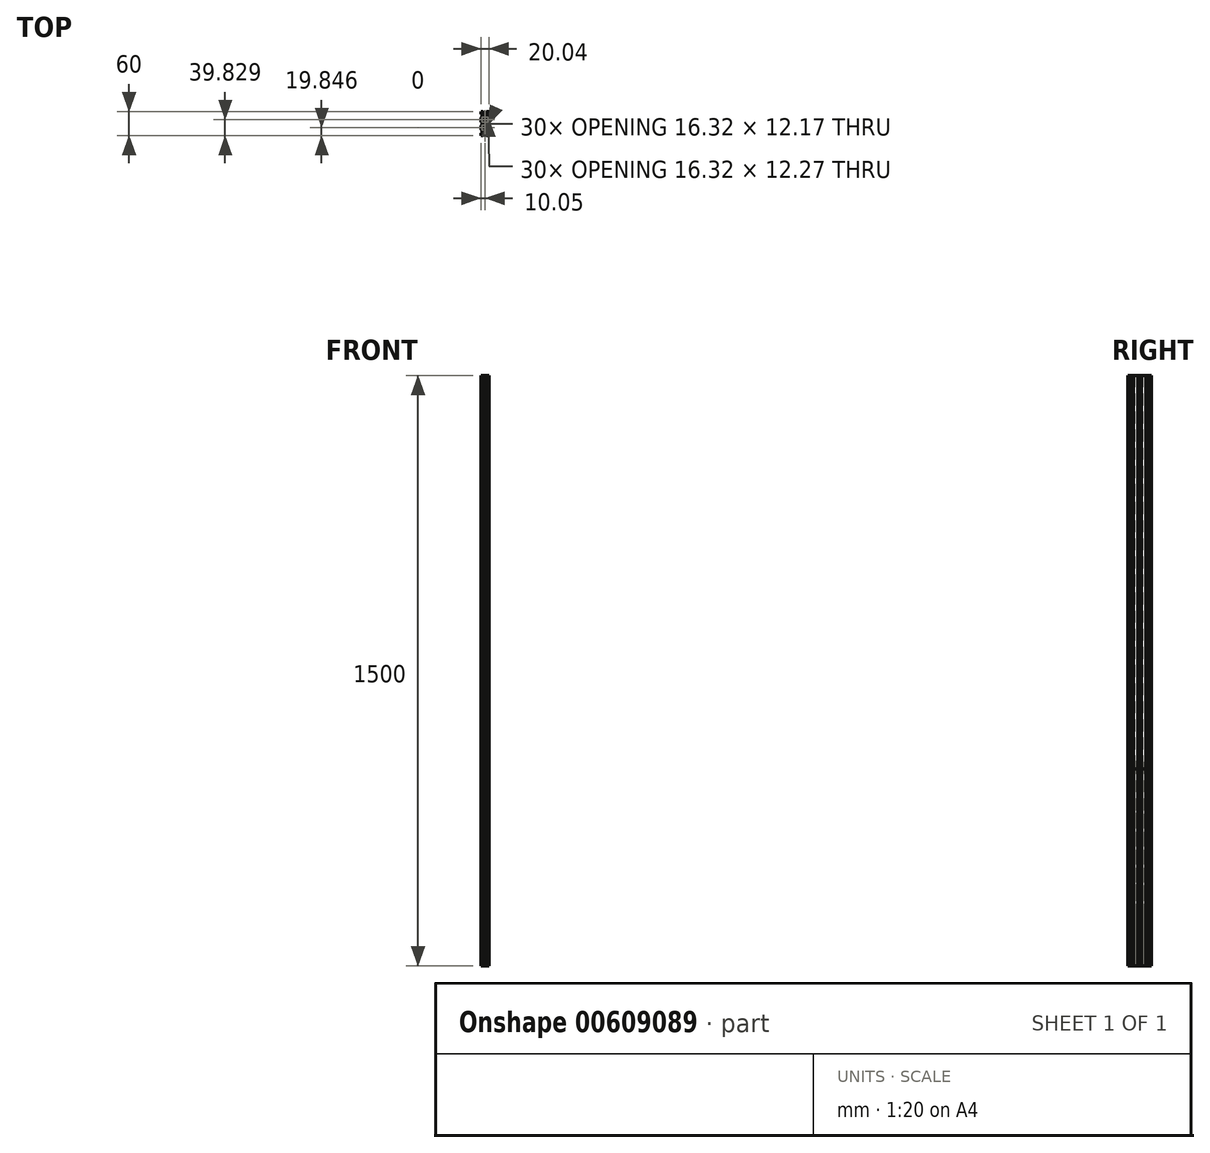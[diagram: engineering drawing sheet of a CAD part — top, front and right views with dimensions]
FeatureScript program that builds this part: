
annotation { "Feature Type Name" : "Feature", "Feature Type Description" : "" }
export const myFeature = defineFeature(function(context is Context, id is Id, definition is map)
    precondition{}
    {
        {
            var Q0;
            Q0=qCreatedBy(makeId("Top.planeOp"),FACE);
            var sketch = newSketch(context, id + "F0", { "sketchPlane" : qUnion([Q0])});
            skLineSegment(sketch, "E0", {"start": v(8.82, 10) * mm, "end": v(5.5, 10) * mm});
            skLineSegment(sketch, "E1", {"start": v(5.5, 10) * mm, "end": v(4.41, 10) * mm});
            skLineSegment(sketch, "E2", {"start": v(4.41, 10) * mm, "end": v(2.4, 8) * mm});
            skLineSegment(sketch, "E3", {"start": v(2.4, 8) * mm, "end": v(5.5, 8) * mm});
            skLineSegment(sketch, "E4", {"start": v(5.5, 8) * mm, "end": v(5.5, 6.68) * mm});
            skLineSegment(sketch, "E5", {"start": v(5.5, 6.68) * mm, "end": v(2.56, 3.74) * mm});
            skLineSegment(sketch, "E6", {"start": v(2.56, 3.74) * mm, "end": v(-2.91, 3.74) * mm});
            skLineSegment(sketch, "E7", {"start": v(-2.91, 3.74) * mm, "end": v(-5.5, 6.33) * mm});
            skLineSegment(sketch, "E8", {"start": v(-5.5, 6.33) * mm, "end": v(-5.5, 8) * mm});
            skLineSegment(sketch, "E9", {"start": v(-5.5, 8) * mm, "end": v(-2.76, 8) * mm});
            skLineSegment(sketch, "E10", {"start": v(-2.76, 8) * mm, "end": v(-4.77, 10) * mm});
            skLineSegment(sketch, "E11", {"start": v(-4.77, 10) * mm, "end": v(-5.5, 10) * mm});
            skLineSegment(sketch, "E12", {"start": v(-5.5, 10) * mm, "end": v(-9.17, 10) * mm});
            skLineSegment(sketch, "E13", {"start": v(-9.17, 10) * mm, "end": v(-10, 10) * mm});
            skLineSegment(sketch, "E14", {"start": v(-10, 10) * mm, "end": v(-10, 8.46) * mm});
            skLineSegment(sketch, "E15", {"start": v(-10, 8.46) * mm, "end": v(-10, 5.5) * mm});
            skLineSegment(sketch, "E16", {"start": v(-10, 5.5) * mm, "end": v(-10, 4.32) * mm});
            skLineSegment(sketch, "E17", {"start": v(-10, 4.32) * mm, "end": v(-8.12, 2.43) * mm});
            skLineSegment(sketch, "E18", {"start": v(-8.12, 2.43) * mm, "end": v(-8.12, 5.5) * mm});
            skLineSegment(sketch, "E19", {"start": v(-8.12, 5.5) * mm, "end": v(-7.05, 5.5) * mm});
            skLineSegment(sketch, "E20", {"start": v(-7.05, 5.5) * mm, "end": v(-3.86, 2.32) * mm});
            skLineSegment(sketch, "E21", {"start": v(-3.86, 2.32) * mm, "end": v(-3.86, -2.68) * mm});
            skLineSegment(sketch, "E22", {"start": v(-3.86, -2.68) * mm, "end": v(-6.68, -5.5) * mm});
            skLineSegment(sketch, "E23", {"start": v(-6.68, -5.5) * mm, "end": v(-8.12, -5.5) * mm});
            skLineSegment(sketch, "E24", {"start": v(-8.12, -5.5) * mm, "end": v(-8.12, -2.8) * mm});
            skLineSegment(sketch, "E25", {"start": v(-8.12, -2.8) * mm, "end": v(-10, -4.68) * mm});
            skLineSegment(sketch, "E26", {"start": v(-10, -4.68) * mm, "end": v(-10, -5.5) * mm});
            skLineSegment(sketch, "E27", {"start": v(-10, -5.5) * mm, "end": v(-10, -8.82) * mm});
            skLineSegment(sketch, "E28", {"start": v(-10, -8.82) * mm, "end": v(-10, -10) * mm});
            skLineSegment(sketch, "E29", {"start": v(-10, -10) * mm, "end": v(-8.8, -10) * mm});
            skLineSegment(sketch, "E30", {"start": v(-8.8, -10) * mm, "end": v(-5.5, -10) * mm});
            skLineSegment(sketch, "E31", {"start": v(-5.5, -10) * mm, "end": v(-4.5, -10) * mm});
            skLineSegment(sketch, "E32", {"start": v(-4.5, -10) * mm, "end": v(-2.85, -8.36) * mm});
            skLineSegment(sketch, "E33", {"start": v(-2.85, -8.36) * mm, "end": v(-5.5, -8.36) * mm});
            skLineSegment(sketch, "E34", {"start": v(-5.5, -8.36) * mm, "end": v(-5.5, -6.7) * mm});
            skLineSegment(sketch, "E35", {"start": v(-5.5, -6.7) * mm, "end": v(-2.82, -4.01) * mm});
            skLineSegment(sketch, "E36", {"start": v(-2.82, -4.01) * mm, "end": v(2.47, -4.01) * mm});
            skLineSegment(sketch, "E37", {"start": v(2.47, -4.01) * mm, "end": v(5.5, -7.05) * mm});
            skLineSegment(sketch, "E38", {"start": v(5.5, -7.05) * mm, "end": v(5.5, -8.36) * mm});
            skLineSegment(sketch, "E39", {"start": v(5.5, -8.36) * mm, "end": v(2.5, -8.36) * mm});
            skLineSegment(sketch, "E40", {"start": v(2.5, -8.36) * mm, "end": v(4.14, -10) * mm});
            skLineSegment(sketch, "E41", {"start": v(4.14, -10) * mm, "end": v(5.5, -10) * mm});
            skLineSegment(sketch, "E42", {"start": v(5.5, -10) * mm, "end": v(8.46, -10) * mm});
            skLineSegment(sketch, "E43", {"start": v(8.46, -10) * mm, "end": v(10, -10) * mm});
            skLineSegment(sketch, "E44", {"start": v(10, -10) * mm, "end": v(10, -9.17) * mm});
            skLineSegment(sketch, "E45", {"start": v(10, -9.17) * mm, "end": v(10, -5.5) * mm});
            skLineSegment(sketch, "E46", {"start": v(10, -5.5) * mm, "end": v(10, -4.6) * mm});
            skLineSegment(sketch, "E47", {"start": v(10, -4.6) * mm, "end": v(8.24, -2.83) * mm});
            skLineSegment(sketch, "E48", {"start": v(8.24, -2.83) * mm, "end": v(8.24, -5.5) * mm});
            skLineSegment(sketch, "E49", {"start": v(8.24, -5.5) * mm, "end": v(6.33, -5.5) * mm});
            skLineSegment(sketch, "E50", {"start": v(6.33, -5.5) * mm, "end": v(3.9, -3.06) * mm});
            skLineSegment(sketch, "E51", {"start": v(3.9, -3.06) * mm, "end": v(3.9, 2.7) * mm});
            skLineSegment(sketch, "E52", {"start": v(3.9, 2.7) * mm, "end": v(6.7, 5.5) * mm});
            skLineSegment(sketch, "E53", {"start": v(6.7, 5.5) * mm, "end": v(8.24, 5.5) * mm});
            skLineSegment(sketch, "E54", {"start": v(8.24, 5.5) * mm, "end": v(8.24, 2.46) * mm});
            skLineSegment(sketch, "E55", {"start": v(8.24, 2.46) * mm, "end": v(10, 4.23) * mm});
            skLineSegment(sketch, "E56", {"start": v(10, 4.23) * mm, "end": v(10, 5.5) * mm});
            skLineSegment(sketch, "E57", {"start": v(10, 5.5) * mm, "end": v(10, 8.8) * mm});
            skLineSegment(sketch, "E58", {"start": v(10, 8.8) * mm, "end": v(10, 10) * mm});
            skLineSegment(sketch, "E59", {"start": v(10, 10) * mm, "end": v(8.82, 10) * mm});
            skSolve(sketch);
        }
        {
            var Q0;
            Q0=makeQuery(id+"F0.imprint","IMPRINT",FACE,{"disambiguationData":[TD([[makeQuery(id+"F0.imprint","IMPRINT",EDGE,{"derivedFrom":sQuery(id+"F0.wireOp",EDGE,"E0")}),1.0]])]});
            extrude(context, id + "F1", {"entities" : qUnion([Q0]), "depth" : 119.7 * mm, "offsetDistance" : 25 * mm});
        }
        {
            var Q0;
            Q0=qCreatedBy(makeId("Top.planeOp"),FACE);
            var sketch = newSketch(context, id + "F2", { "sketchPlane" : qUnion([Q0])});
            skLineSegment(sketch, "E60", {"start": v(8.84, 30) * mm, "end": v(5.51, 30) * mm});
            skLineSegment(sketch, "E61", {"start": v(5.51, 30) * mm, "end": v(4.42, 30) * mm});
            skLineSegment(sketch, "E62", {"start": v(4.42, 30) * mm, "end": v(2.41, 28) * mm});
            skLineSegment(sketch, "E63", {"start": v(2.41, 28) * mm, "end": v(5.51, 28) * mm});
            skLineSegment(sketch, "E64", {"start": v(5.51, 28) * mm, "end": v(5.51, 26.67) * mm});
            skLineSegment(sketch, "E65", {"start": v(5.51, 26.67) * mm, "end": v(2.56, 23.73) * mm});
            skLineSegment(sketch, "E66", {"start": v(2.56, 23.73) * mm, "end": v(-2.92, 23.73) * mm});
            skLineSegment(sketch, "E67", {"start": v(-2.92, 23.73) * mm, "end": v(-5.51, 26.32) * mm});
            skLineSegment(sketch, "E68", {"start": v(-5.51, 26.32) * mm, "end": v(-5.51, 28) * mm});
            skLineSegment(sketch, "E69", {"start": v(-5.51, 28) * mm, "end": v(-2.76, 28) * mm});
            skLineSegment(sketch, "E70", {"start": v(-2.76, 28) * mm, "end": v(-4.77, 30) * mm});
            skLineSegment(sketch, "E71", {"start": v(-4.77, 30) * mm, "end": v(-5.51, 30) * mm});
            skLineSegment(sketch, "E72", {"start": v(-5.51, 30) * mm, "end": v(-9.19, 30) * mm});
            skLineSegment(sketch, "E73", {"start": v(-9.19, 30) * mm, "end": v(-10.02, 30) * mm});
            skLineSegment(sketch, "E74", {"start": v(-10.02, 30) * mm, "end": v(-10.02, 28.45) * mm});
            skLineSegment(sketch, "E75", {"start": v(-10.02, 28.45) * mm, "end": v(-10.02, 25.5) * mm});
            skLineSegment(sketch, "E76", {"start": v(-10.02, 25.5) * mm, "end": v(-10.02, 24.3) * mm});
            skLineSegment(sketch, "E77", {"start": v(-10.02, 24.3) * mm, "end": v(-8.13, 22.42) * mm});
            skLineSegment(sketch, "E78", {"start": v(-8.13, 22.42) * mm, "end": v(-8.13, 25.5) * mm});
            skLineSegment(sketch, "E79", {"start": v(-8.13, 25.5) * mm, "end": v(-7.06, 25.5) * mm});
            skLineSegment(sketch, "E80", {"start": v(-7.06, 25.5) * mm, "end": v(-3.87, 22.3) * mm});
            skLineSegment(sketch, "E81", {"start": v(-3.87, 22.3) * mm, "end": v(-3.87, 17.3) * mm});
            skLineSegment(sketch, "E82", {"start": v(-3.87, 17.3) * mm, "end": v(-6.7, 14.47) * mm});
            skLineSegment(sketch, "E83", {"start": v(-6.7, 14.47) * mm, "end": v(-8.13, 14.47) * mm});
            skLineSegment(sketch, "E84", {"start": v(-8.13, 14.47) * mm, "end": v(-8.13, 17.18) * mm});
            skLineSegment(sketch, "E85", {"start": v(-8.13, 17.18) * mm, "end": v(-10.02, 15.3) * mm});
            skLineSegment(sketch, "E86", {"start": v(-10.02, 15.3) * mm, "end": v(-10.02, 14.47) * mm});
            skLineSegment(sketch, "E87", {"start": v(-10.02, 14.47) * mm, "end": v(-10.02, 11.15) * mm});
            skLineSegment(sketch, "E88", {"start": v(-10.02, 11.15) * mm, "end": v(-10.02, 9.97) * mm});
            skLineSegment(sketch, "E89", {"start": v(-10.02, 9.97) * mm, "end": v(-10.02, 8.42) * mm});
            skLineSegment(sketch, "E90", {"start": v(-10.02, 8.42) * mm, "end": v(-10.02, 5.46) * mm});
            skLineSegment(sketch, "E91", {"start": v(-10.02, 5.46) * mm, "end": v(-10.02, 4.27) * mm});
            skLineSegment(sketch, "E92", {"start": v(-10.02, 4.27) * mm, "end": v(-8.13, 2.38) * mm});
            skLineSegment(sketch, "E93", {"start": v(-8.13, 2.38) * mm, "end": v(-8.13, 5.46) * mm});
            skLineSegment(sketch, "E94", {"start": v(-8.13, 5.46) * mm, "end": v(-7.06, 5.46) * mm});
            skLineSegment(sketch, "E95", {"start": v(-7.06, 5.46) * mm, "end": v(-3.87, 2.27) * mm});
            skLineSegment(sketch, "E96", {"start": v(-3.87, 2.27) * mm, "end": v(-3.87, -2.74) * mm});
            skLineSegment(sketch, "E97", {"start": v(-3.87, -2.74) * mm, "end": v(-6.7, -5.56) * mm});
            skLineSegment(sketch, "E98", {"start": v(-6.7, -5.56) * mm, "end": v(-8.13, -5.56) * mm});
            skLineSegment(sketch, "E99", {"start": v(-8.13, -5.56) * mm, "end": v(-8.13, -2.85) * mm});
            skLineSegment(sketch, "E100", {"start": v(-8.13, -2.85) * mm, "end": v(-10.02, -4.74) * mm});
            skLineSegment(sketch, "E101", {"start": v(-10.02, -4.74) * mm, "end": v(-10.02, -5.56) * mm});
            skLineSegment(sketch, "E102", {"start": v(-10.02, -5.56) * mm, "end": v(-10.02, -8.89) * mm});
            skLineSegment(sketch, "E103", {"start": v(-10.02, -8.89) * mm, "end": v(-10.02, -9.97) * mm});
            skLineSegment(sketch, "E104", {"start": v(-10.02, -9.97) * mm, "end": v(-10.02, -10.07) * mm});
            skLineSegment(sketch, "E105", {"start": v(-10.02, -10.07) * mm, "end": v(-10.02, -11.51) * mm});
            skLineSegment(sketch, "E106", {"start": v(-10.02, -11.51) * mm, "end": v(-10.02, -14.47) * mm});
            skLineSegment(sketch, "E107", {"start": v(-10.02, -14.47) * mm, "end": v(-10.02, -15.66) * mm});
            skLineSegment(sketch, "E108", {"start": v(-10.02, -15.66) * mm, "end": v(-8.13, -17.55) * mm});
            skLineSegment(sketch, "E109", {"start": v(-8.13, -17.55) * mm, "end": v(-8.13, -14.47) * mm});
            skLineSegment(sketch, "E110", {"start": v(-8.13, -14.47) * mm, "end": v(-7.06, -14.47) * mm});
            skLineSegment(sketch, "E111", {"start": v(-7.06, -14.47) * mm, "end": v(-3.87, -17.66) * mm});
            skLineSegment(sketch, "E112", {"start": v(-3.87, -17.66) * mm, "end": v(-3.87, -22.67) * mm});
            skLineSegment(sketch, "E113", {"start": v(-3.87, -22.67) * mm, "end": v(-6.7, -25.5) * mm});
            skLineSegment(sketch, "E114", {"start": v(-6.7, -25.5) * mm, "end": v(-8.13, -25.5) * mm});
            skLineSegment(sketch, "E115", {"start": v(-8.13, -25.5) * mm, "end": v(-8.13, -22.78) * mm});
            skLineSegment(sketch, "E116", {"start": v(-8.13, -22.78) * mm, "end": v(-10.02, -24.67) * mm});
            skLineSegment(sketch, "E117", {"start": v(-10.02, -24.67) * mm, "end": v(-10.02, -25.5) * mm});
            skLineSegment(sketch, "E118", {"start": v(-10.02, -25.5) * mm, "end": v(-10.02, -28.82) * mm});
            skLineSegment(sketch, "E119", {"start": v(-10.02, -28.82) * mm, "end": v(-10.02, -30) * mm});
            skLineSegment(sketch, "E120", {"start": v(-10.02, -30) * mm, "end": v(-8.82, -30) * mm});
            skLineSegment(sketch, "E121", {"start": v(-8.82, -30) * mm, "end": v(-5.51, -30) * mm});
            skLineSegment(sketch, "E122", {"start": v(-5.51, -30) * mm, "end": v(-4.5, -30) * mm});
            skLineSegment(sketch, "E123", {"start": v(-4.5, -30) * mm, "end": v(-2.86, -28.36) * mm});
            skLineSegment(sketch, "E124", {"start": v(-2.86, -28.36) * mm, "end": v(-5.51, -28.36) * mm});
            skLineSegment(sketch, "E125", {"start": v(-5.51, -28.36) * mm, "end": v(-5.51, -26.69) * mm});
            skLineSegment(sketch, "E126", {"start": v(-5.51, -26.69) * mm, "end": v(-2.83, -24) * mm});
            skLineSegment(sketch, "E127", {"start": v(-2.83, -24) * mm, "end": v(2.47, -24) * mm});
            skLineSegment(sketch, "E128", {"start": v(2.47, -24) * mm, "end": v(5.51, -27.04) * mm});
            skLineSegment(sketch, "E129", {"start": v(5.51, -27.04) * mm, "end": v(5.51, -28.36) * mm});
            skLineSegment(sketch, "E130", {"start": v(5.51, -28.36) * mm, "end": v(2.5, -28.36) * mm});
            skLineSegment(sketch, "E131", {"start": v(2.5, -28.36) * mm, "end": v(4.15, -30) * mm});
            skLineSegment(sketch, "E132", {"start": v(4.15, -30) * mm, "end": v(5.51, -30) * mm});
            skLineSegment(sketch, "E133", {"start": v(5.51, -30) * mm, "end": v(8.47, -30) * mm});
            skLineSegment(sketch, "E134", {"start": v(8.47, -30) * mm, "end": v(10.02, -30) * mm});
            skLineSegment(sketch, "E135", {"start": v(10.02, -30) * mm, "end": v(10.02, -29.17) * mm});
            skLineSegment(sketch, "E136", {"start": v(10.02, -29.17) * mm, "end": v(10.02, -25.5) * mm});
            skLineSegment(sketch, "E137", {"start": v(10.02, -25.5) * mm, "end": v(10.02, -24.58) * mm});
            skLineSegment(sketch, "E138", {"start": v(10.02, -24.58) * mm, "end": v(8.25, -22.82) * mm});
            skLineSegment(sketch, "E139", {"start": v(8.25, -22.82) * mm, "end": v(8.25, -25.5) * mm});
            skLineSegment(sketch, "E140", {"start": v(8.25, -25.5) * mm, "end": v(6.34, -25.5) * mm});
            skLineSegment(sketch, "E141", {"start": v(6.34, -25.5) * mm, "end": v(3.9, -23.05) * mm});
            skLineSegment(sketch, "E142", {"start": v(3.9, -23.05) * mm, "end": v(3.9, -17.28) * mm});
            skLineSegment(sketch, "E143", {"start": v(3.9, -17.28) * mm, "end": v(6.7, -14.47) * mm});
            skLineSegment(sketch, "E144", {"start": v(6.7, -14.47) * mm, "end": v(8.25, -14.47) * mm});
            skLineSegment(sketch, "E145", {"start": v(8.25, -14.47) * mm, "end": v(8.25, -17.51) * mm});
            skLineSegment(sketch, "E146", {"start": v(8.25, -17.51) * mm, "end": v(10.02, -15.75) * mm});
            skLineSegment(sketch, "E147", {"start": v(10.02, -15.75) * mm, "end": v(10.02, -14.47) * mm});
            skLineSegment(sketch, "E148", {"start": v(10.02, -14.47) * mm, "end": v(10.02, -11.16) * mm});
            skLineSegment(sketch, "E149", {"start": v(10.02, -11.16) * mm, "end": v(10.02, -10.07) * mm});
            skLineSegment(sketch, "E150", {"start": v(10.02, -10.07) * mm, "end": v(10.02, -9.97) * mm});
            skLineSegment(sketch, "E151", {"start": v(10.02, -9.97) * mm, "end": v(10.02, -9.24) * mm});
            skLineSegment(sketch, "E152", {"start": v(10.02, -9.24) * mm, "end": v(10.02, -5.56) * mm});
            skLineSegment(sketch, "E153", {"start": v(10.02, -5.56) * mm, "end": v(10.02, -4.65) * mm});
            skLineSegment(sketch, "E154", {"start": v(10.02, -4.65) * mm, "end": v(8.25, -2.88) * mm});
            skLineSegment(sketch, "E155", {"start": v(8.25, -2.88) * mm, "end": v(8.25, -5.56) * mm});
            skLineSegment(sketch, "E156", {"start": v(8.25, -5.56) * mm, "end": v(6.34, -5.56) * mm});
            skLineSegment(sketch, "E157", {"start": v(6.34, -5.56) * mm, "end": v(3.9, -3.12) * mm});
            skLineSegment(sketch, "E158", {"start": v(3.9, -3.12) * mm, "end": v(3.9, 2.65) * mm});
            skLineSegment(sketch, "E159", {"start": v(3.9, 2.65) * mm, "end": v(6.7, 5.46) * mm});
            skLineSegment(sketch, "E160", {"start": v(6.7, 5.46) * mm, "end": v(8.25, 5.46) * mm});
            skLineSegment(sketch, "E161", {"start": v(8.25, 5.46) * mm, "end": v(8.25, 2.42) * mm});
            skLineSegment(sketch, "E162", {"start": v(8.25, 2.42) * mm, "end": v(10.02, 4.18) * mm});
            skLineSegment(sketch, "E163", {"start": v(10.02, 4.18) * mm, "end": v(10.02, 5.46) * mm});
            skLineSegment(sketch, "E164", {"start": v(10.02, 5.46) * mm, "end": v(10.02, 8.77) * mm});
            skLineSegment(sketch, "E165", {"start": v(10.02, 8.77) * mm, "end": v(10.02, 9.97) * mm});
            skLineSegment(sketch, "E166", {"start": v(10.02, 9.97) * mm, "end": v(10.02, 10.8) * mm});
            skLineSegment(sketch, "E167", {"start": v(10.02, 10.8) * mm, "end": v(10.02, 14.47) * mm});
            skLineSegment(sketch, "E168", {"start": v(10.02, 14.47) * mm, "end": v(10.02, 15.38) * mm});
            skLineSegment(sketch, "E169", {"start": v(10.02, 15.38) * mm, "end": v(8.25, 17.15) * mm});
            skLineSegment(sketch, "E170", {"start": v(8.25, 17.15) * mm, "end": v(8.25, 14.47) * mm});
            skLineSegment(sketch, "E171", {"start": v(8.25, 14.47) * mm, "end": v(6.34, 14.47) * mm});
            skLineSegment(sketch, "E172", {"start": v(6.34, 14.47) * mm, "end": v(3.9, 16.91) * mm});
            skLineSegment(sketch, "E173", {"start": v(3.9, 16.91) * mm, "end": v(3.9, 22.69) * mm});
            skLineSegment(sketch, "E174", {"start": v(3.9, 22.69) * mm, "end": v(6.7, 25.5) * mm});
            skLineSegment(sketch, "E175", {"start": v(6.7, 25.5) * mm, "end": v(8.25, 25.5) * mm});
            skLineSegment(sketch, "E176", {"start": v(8.25, 25.5) * mm, "end": v(8.25, 22.45) * mm});
            skLineSegment(sketch, "E177", {"start": v(8.25, 22.45) * mm, "end": v(10.02, 24.22) * mm});
            skLineSegment(sketch, "E178", {"start": v(10.02, 24.22) * mm, "end": v(10.02, 25.5) * mm});
            skLineSegment(sketch, "E179", {"start": v(10.02, 25.5) * mm, "end": v(10.02, 28.8) * mm});
            skLineSegment(sketch, "E180", {"start": v(10.02, 28.8) * mm, "end": v(10.02, 30) * mm});
            skLineSegment(sketch, "E181", {"start": v(10.02, 30) * mm, "end": v(8.84, 30) * mm});
            skLineSegment(sketch, "E182", {"start": v(5.51, -7.1) * mm, "end": v(5.51, -7.3) * mm});
            skLineSegment(sketch, "E183", {"start": v(5.51, -7.3) * mm, "end": v(8.2, -7.3) * mm});
            skLineSegment(sketch, "E184", {"start": v(8.2, -7.3) * mm, "end": v(8.2, -12.83) * mm});
            skLineSegment(sketch, "E185", {"start": v(8.2, -12.83) * mm, "end": v(5.51, -12.83) * mm});
            skLineSegment(sketch, "E186", {"start": v(5.51, -12.83) * mm, "end": v(5.51, -13.3) * mm});
            skLineSegment(sketch, "E187", {"start": v(5.51, -13.3) * mm, "end": v(2.56, -16.24) * mm});
            skLineSegment(sketch, "E188", {"start": v(2.56, -16.24) * mm, "end": v(-2.92, -16.24) * mm});
            skLineSegment(sketch, "E189", {"start": v(-2.92, -16.24) * mm, "end": v(-5.51, -13.64) * mm});
            skLineSegment(sketch, "E190", {"start": v(-5.51, -13.64) * mm, "end": v(-5.51, -12.83) * mm});
            skLineSegment(sketch, "E191", {"start": v(-5.51, -12.83) * mm, "end": v(-8.13, -12.83) * mm});
            skLineSegment(sketch, "E192", {"start": v(-8.13, -12.83) * mm, "end": v(-8.13, -7.3) * mm});
            skLineSegment(sketch, "E193", {"start": v(-8.13, -7.3) * mm, "end": v(-5.51, -7.3) * mm});
            skLineSegment(sketch, "E194", {"start": v(-5.51, -7.3) * mm, "end": v(-5.51, -6.75) * mm});
            skLineSegment(sketch, "E195", {"start": v(-5.51, -6.75) * mm, "end": v(-2.83, -4.07) * mm});
            skLineSegment(sketch, "E196", {"start": v(-2.83, -4.07) * mm, "end": v(2.47, -4.07) * mm});
            skLineSegment(sketch, "E197", {"start": v(2.47, -4.07) * mm, "end": v(5.51, -7.1) * mm});
            skLineSegment(sketch, "E198", {"start": v(5.51, 12.93) * mm, "end": v(5.51, 12.7) * mm});
            skLineSegment(sketch, "E199", {"start": v(5.51, 12.7) * mm, "end": v(8.2, 12.7) * mm});
            skLineSegment(sketch, "E200", {"start": v(8.2, 12.7) * mm, "end": v(8.2, 7.19) * mm});
            skLineSegment(sketch, "E201", {"start": v(8.2, 7.19) * mm, "end": v(5.51, 7.19) * mm});
            skLineSegment(sketch, "E202", {"start": v(5.51, 7.19) * mm, "end": v(5.51, 6.64) * mm});
            skLineSegment(sketch, "E203", {"start": v(5.51, 6.64) * mm, "end": v(2.56, 3.7) * mm});
            skLineSegment(sketch, "E204", {"start": v(2.56, 3.7) * mm, "end": v(-2.92, 3.7) * mm});
            skLineSegment(sketch, "E205", {"start": v(-2.92, 3.7) * mm, "end": v(-5.51, 6.29) * mm});
            skLineSegment(sketch, "E206", {"start": v(-5.51, 6.29) * mm, "end": v(-5.51, 7.19) * mm});
            skLineSegment(sketch, "E207", {"start": v(-5.51, 7.19) * mm, "end": v(-8.13, 7.19) * mm});
            skLineSegment(sketch, "E208", {"start": v(-8.13, 7.19) * mm, "end": v(-8.13, 12.7) * mm});
            skLineSegment(sketch, "E209", {"start": v(-8.13, 12.7) * mm, "end": v(-5.51, 12.7) * mm});
            skLineSegment(sketch, "E210", {"start": v(-5.51, 12.7) * mm, "end": v(-5.51, 13.28) * mm});
            skLineSegment(sketch, "E211", {"start": v(-5.51, 13.28) * mm, "end": v(-2.83, 15.96) * mm});
            skLineSegment(sketch, "E212", {"start": v(-2.83, 15.96) * mm, "end": v(2.47, 15.96) * mm});
            skLineSegment(sketch, "E213", {"start": v(2.47, 15.96) * mm, "end": v(5.51, 12.93) * mm});
            skSolve(sketch);
        }
        {
            var Q0;
            Q0=makeQuery(id+"F2.imprint","IMPRINT",FACE,{"disambiguationData":[TD([[makeQuery(id+"F2.imprint","IMPRINT",EDGE,{"derivedFrom":sQuery(id+"F2.wireOp",EDGE,"E60")}),1.0]])]});
            extrude(context, id + "F3", {"entities" : qUnion([Q0]), "depth" : 1500 * mm, "offsetDistance" : 25 * mm});
        }
        {
            var Q0;
            Q0=makeQuery(id+"F0.imprint","IMPRINT",FACE,{"disambiguationData":[TD([[makeQuery(id+"F0.imprint","IMPRINT",EDGE,{"derivedFrom":sQuery(id+"F0.wireOp",EDGE,"E0")}),1.0]])]});
            extrude(context, id + "F4", {"entities" : qUnion([Q0]), "depth" : 203.8 * mm, "offsetDistance" : 25 * mm});
        }
        {
            var Q0;
            Q0=makeQuery(id+"F0.imprint","IMPRINT",FACE,{"disambiguationData":[TD([[makeQuery(id+"F0.imprint","IMPRINT",EDGE,{"derivedFrom":sQuery(id+"F0.wireOp",EDGE,"E0")}),1.0]])]});
            extrude(context, id + "F5", {"entities" : qUnion([Q0]), "depth" : 287.6 * mm, "offsetDistance" : 25 * mm});
        }
        {
            var Q0;
            Q0=makeQuery(id+"F0.imprint","IMPRINT",FACE,{"disambiguationData":[TD([[makeQuery(id+"F0.imprint","IMPRINT",EDGE,{"derivedFrom":sQuery(id+"F0.wireOp",EDGE,"E0")}),1.0]])]});
            extrude(context, id + "F6", {"entities" : qUnion([Q0]), "depth" : 386.6 * mm, "offsetDistance" : 25 * mm});
        }
        {
            var Q0;
            Q0=makeQuery(id+"F0.imprint","IMPRINT",FACE,{"disambiguationData":[TD([[makeQuery(id+"F0.imprint","IMPRINT",EDGE,{"derivedFrom":sQuery(id+"F0.wireOp",EDGE,"E0")}),1.0]])]});
            extrude(context, id + "F7", {"entities" : qUnion([Q0]), "depth" : 517.5 * mm, "offsetDistance" : 25 * mm});
        }
        {
            var Q0;
            Q0=makeQuery(id+"F2.imprint","IMPRINT",FACE,{"disambiguationData":[TD([[makeQuery(id+"F2.imprint","IMPRINT",EDGE,{"derivedFrom":sQuery(id+"F2.wireOp",EDGE,"E60")}),1.0]])]});
            extrude(context, id + "F8", {"entities" : qUnion([Q0]), "depth" : 500 * mm, "offsetDistance" : 25 * mm});
        }
    });
